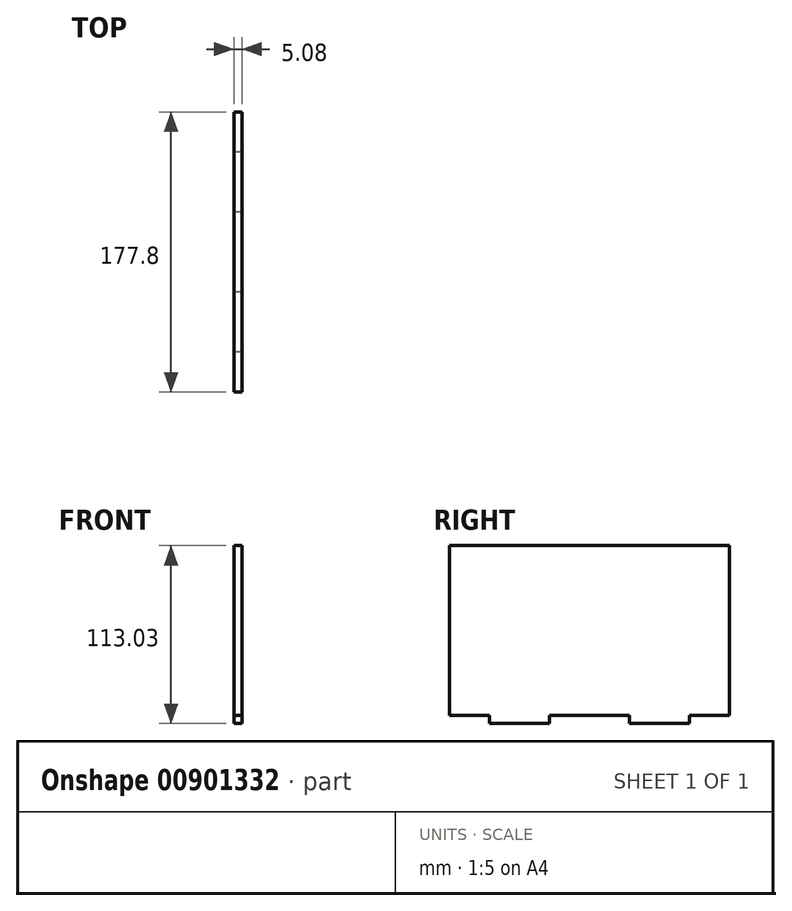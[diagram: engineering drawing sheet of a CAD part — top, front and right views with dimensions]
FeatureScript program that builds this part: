
annotation { "Feature Type Name" : "Feature", "Feature Type Description" : "" }
export const myFeature = defineFeature(function(context is Context, id is Id, definition is map)
    precondition{}
    {
        {
            var Q0;
            Q0=qCreatedBy(makeId("Right.planeOp"),FACE);
            var sketch = newSketch(context, id + "F0", { "sketchPlane" : qUnion([Q0])});
            skLineSegment(sketch, "E0", {"start": v(0, 0.1) * mm, "end": v(-25.4, 0.1) * mm});
            skLineSegment(sketch, "E1", {"start": v(-25.4, 0.1) * mm, "end": v(-25.4, -4.99) * mm});
            skLineSegment(sketch, "E2", {"start": v(-25.4, -4.99) * mm, "end": v(-63.5, -4.99) * mm});
            skLineSegment(sketch, "E3", {"start": v(-63.5, -4.99) * mm, "end": v(-63.5, 0.1) * mm});
            skLineSegment(sketch, "E4.MirrorCS", {"start": v(0, 0.1) * mm, "end": v(25.4, 0.1) * mm});
            skLineSegment(sketch, "E5.MirrorCS", {"start": v(25.4, 0.1) * mm, "end": v(25.4, -4.99) * mm});
            skLineSegment(sketch, "E6.MirrorCS", {"start": v(25.4, -4.99) * mm, "end": v(63.5, -4.99) * mm});
            skLineSegment(sketch, "E7.MirrorCS", {"start": v(63.5, -4.99) * mm, "end": v(63.5, 0.1) * mm});
            skLineSegment(sketch, "E8", {"start": v(-88.9, 6.44) * mm, "end": v(-88.9, 108.04) * mm});
            skLineSegment(sketch, "E9", {"start": v(88.9, 6.44) * mm, "end": v(88.9, 108.04) * mm});
            skLineSegment(sketch, "E10", {"start": v(-88.9, 108.04) * mm, "end": v(88.9, 108.04) * mm});
            skLineSegment(sketch, "E11", {"start": v(-88.9, 6.44) * mm, "end": v(-88.9, 0) * mm});
            skLineSegment(sketch, "E12", {"start": v(-88.9, 0) * mm, "end": v(-63.5, 0.1) * mm});
            skLineSegment(sketch, "E13", {"start": v(88.9, 6.44) * mm, "end": v(88.9, 0) * mm});
            skLineSegment(sketch, "E14", {"start": v(88.9, 0) * mm, "end": v(63.5, 0.1) * mm});
            skSolve(sketch);
        }
        {
            var Q0;
            Q0=makeQuery(id+"F0.imprint","IMPRINT",FACE,{"disambiguationData":[TD([[makeQuery(id+"F0.imprint","IMPRINT",EDGE,{"derivedFrom":sQuery(id+"F0.wireOp",EDGE,"E0")}),-1.0]])]});
            extrude(context, id + "F1", {"entities" : qUnion([Q0]), "depth" : 5.08 * mm, "offsetDistance" : 25.4 * mm});
        }
    });
